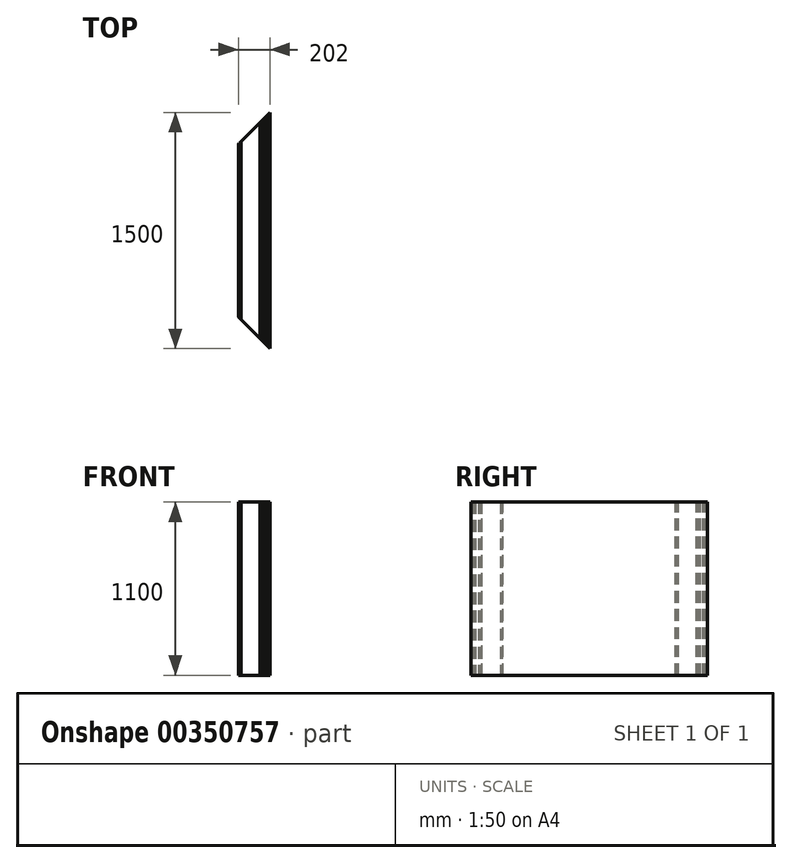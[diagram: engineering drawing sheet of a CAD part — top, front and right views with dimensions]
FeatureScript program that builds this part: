
annotation { "Feature Type Name" : "Feature", "Feature Type Description" : "" }
export const myFeature = defineFeature(function(context is Context, id is Id, definition is map)
    precondition{}
    {
        {
            var Q0;
            Q0=qCreatedBy(makeId("Right.planeOp"),FACE);
            var sketch = newSketch(context, id + "F0", { "sketchPlane" : qUnion([Q0])});
            skLineSegment(sketch, "E0", {"start": v(0, 0) * mm, "end": v(1500, 0) * mm});
            skLineSegment(sketch, "E1", {"start": v(1500, 0) * mm, "end": v(1500, 1100) * mm});
            skLineSegment(sketch, "E2", {"start": v(1500, 1100) * mm, "end": v(0, 1100) * mm});
            skLineSegment(sketch, "E3", {"start": v(0, 1100) * mm, "end": v(0, 0) * mm});
            skSolve(sketch);
        }
        {
            var Q0;
            Q0=makeQuery(id+"F0.imprint","IMPRINT",FACE,{"disambiguationData":[TD([[makeQuery(id+"F0.imprint","IMPRINT",EDGE,{"derivedFrom":sQuery(id+"F0.wireOp",EDGE,"E0")}),1.0]])]});
            extrude(context, id + "F1", {"entities" : qUnion([Q0]), "depth" : 6 * mm});
        }
        {
            var Q0;
            Q0=makeQuery(id+"F1.opExtrude","CAP_FACE",FACE,{"disambiguationData":[OSD([sQuery(id+"F0.wireOp",EDGE,"E0"),sQuery(id+"F0.wireOp",EDGE,"E1"),sQuery(id+"F0.wireOp",EDGE,"E2"),sQuery(id+"F0.wireOp",EDGE,"UxQu33BP-PdVc-IvKo-0Oal-Oq9sfbCTzBfW"),sQuery(id+"F0.wireOp",EDGE,"E3")])],"isStart":false});
            extrude(context, id + "F2", {"entities" : qUnion([Q0]), "depth" : 1 * mm});
        }
        {
            var Q0;
            Q0=makeQuery(id+"F2.opExtrude","CAP_FACE",FACE,{"disambiguationData":[OSD([sQuery(id+"F0.wireOp",EDGE,"E0"),sQuery(id+"F0.wireOp",EDGE,"E1"),sQuery(id+"F0.wireOp",EDGE,"E2"),sQuery(id+"F0.wireOp",EDGE,"UxQu33BP-PdVc-IvKo-0Oal-Oq9sfbCTzBfW"),sQuery(id+"F0.wireOp",EDGE,"E3")])],"isStart":false});
            extrude(context, id + "F3", {"entities" : qUnion([Q0]), "depth" : 10 * mm});
        }
        {
            var Q0;
            Q0=makeQuery(id+"F3.opExtrude","CAP_FACE",FACE,{"disambiguationData":[OSD([sQuery(id+"F0.wireOp",EDGE,"E0"),sQuery(id+"F0.wireOp",EDGE,"E1"),sQuery(id+"F0.wireOp",EDGE,"E2"),sQuery(id+"F0.wireOp",EDGE,"UxQu33BP-PdVc-IvKo-0Oal-Oq9sfbCTzBfW"),sQuery(id+"F0.wireOp",EDGE,"E3")])],"isStart":false});
            extrude(context, id + "F4", {"entities" : qUnion([Q0]), "depth" : 120 * mm});
        }
        {
            var Q0;
            Q0=makeQuery(id+"F4.opExtrude","CAP_FACE",FACE,{"disambiguationData":[OSD([sQuery(id+"F0.wireOp",EDGE,"E0"),sQuery(id+"F0.wireOp",EDGE,"E1"),sQuery(id+"F0.wireOp",EDGE,"E2"),sQuery(id+"F0.wireOp",EDGE,"UxQu33BP-PdVc-IvKo-0Oal-Oq9sfbCTzBfW"),sQuery(id+"F0.wireOp",EDGE,"E3")])],"isStart":false});
            extrude(context, id + "F5", {"entities" : qUnion([Q0]), "depth" : 10 * mm});
        }
        {
            var Q0;
            Q0=makeQuery(id+"F5.opExtrude","CAP_FACE",FACE,{"disambiguationData":[OSD([sQuery(id+"F0.wireOp",EDGE,"E0"),sQuery(id+"F0.wireOp",EDGE,"E1"),sQuery(id+"F0.wireOp",EDGE,"E2"),sQuery(id+"F0.wireOp",EDGE,"UxQu33BP-PdVc-IvKo-0Oal-Oq9sfbCTzBfW"),sQuery(id+"F0.wireOp",EDGE,"E3")])],"isStart":false});
            extrude(context, id + "F6", {"entities" : qUnion([Q0]), "depth" : 10 * mm});
        }
        {
            var Q0;
            Q0=makeQuery(id+"F6.opExtrude","CAP_FACE",FACE,{"disambiguationData":[OSD([sQuery(id+"F0.wireOp",EDGE,"E0"),sQuery(id+"F0.wireOp",EDGE,"E1"),sQuery(id+"F0.wireOp",EDGE,"E2"),sQuery(id+"F0.wireOp",EDGE,"UxQu33BP-PdVc-IvKo-0Oal-Oq9sfbCTzBfW"),sQuery(id+"F0.wireOp",EDGE,"E3")])],"isStart":false});
            extrude(context, id + "F7", {"entities" : qUnion([Q0]), "depth" : 18 * mm});
        }
        {
            var Q0;
            Q0=makeQuery(id+"F7.opExtrude","CAP_FACE",FACE,{"disambiguationData":[OSD([sQuery(id+"F0.wireOp",EDGE,"E0"),sQuery(id+"F0.wireOp",EDGE,"E1"),sQuery(id+"F0.wireOp",EDGE,"E2"),sQuery(id+"F0.wireOp",EDGE,"UxQu33BP-PdVc-IvKo-0Oal-Oq9sfbCTzBfW"),sQuery(id+"F0.wireOp",EDGE,"E3")])],"isStart":false});
            extrude(context, id + "F8", {"entities" : qUnion([Q0]), "depth" : 10 * mm});
        }
        {
            var Q0;
            Q0=makeQuery(id+"F8.opExtrude","CAP_FACE",FACE,{"disambiguationData":[OSD([sQuery(id+"F0.wireOp",EDGE,"E0"),sQuery(id+"F0.wireOp",EDGE,"E1"),sQuery(id+"F0.wireOp",EDGE,"E2"),sQuery(id+"F0.wireOp",EDGE,"E3")])],"isStart":false});
            extrude(context, id + "F9", {"entities" : qUnion([Q0]), "depth" : 1 * mm});
        }
        {
            var Q0;
            Q0=makeQuery(id+"F9.opExtrude","CAP_FACE",FACE,{"disambiguationData":[OSD([sQuery(id+"F0.wireOp",EDGE,"E0"),sQuery(id+"F0.wireOp",EDGE,"E1"),sQuery(id+"F0.wireOp",EDGE,"E2"),sQuery(id+"F0.wireOp",EDGE,"E3")])],"isStart":false});
            var sketch = newSketch(context, id + "F10", { "sketchPlane" : qUnion([Q0])});
            skLineSegment(sketch, "E4.bottom", {"start": v(0, 0) * mm, "end": v(70, 0) * mm});
            skLineSegment(sketch, "E4.top", {"start": v(0, 1100) * mm, "end": v(70, 1100) * mm});
            skLineSegment(sketch, "E4.left", {"start": v(0, 0) * mm, "end": v(0, 1100) * mm});
            skLineSegment(sketch, "E4.right", {"start": v(70, 0) * mm, "end": v(70, 1100) * mm});
            skLineSegment(sketch, "E5.bottom", {"start": v(1500, 0) * mm, "end": v(1430, 0) * mm});
            skLineSegment(sketch, "E5.top", {"start": v(1500, 1100) * mm, "end": v(1430, 1100) * mm});
            skLineSegment(sketch, "E5.left", {"start": v(1500, 0) * mm, "end": v(1500, 1100) * mm});
            skLineSegment(sketch, "E5.right", {"start": v(1430, 0) * mm, "end": v(1430, 1100) * mm});
            skSolve(sketch);
        }
        {
            var Q0;
            Q0 = qSketchRegion(id + "F10", true);
            extrude(context, id + "F11", {"entities" : qUnion([Q0]), "depth" : 8 * mm});
        }
        {
            var Q0;
            Q0=makeQuery(id+"F11.opExtrude","CAP_FACE",FACE,{"disambiguationData":[OSD([sQuery(id+"F10.wireOp",EDGE,"E4.bottom"),sQuery(id+"F10.wireOp",EDGE,"E4.top"),sQuery(id+"F10.wireOp",EDGE,"E4.left"),sQuery(id+"F10.wireOp",EDGE,"E4.right")])],"isStart":false});
            var sketch = newSketch(context, id + "F12", { "sketchPlane" : qUnion([Q0])});
            skLineSegment(sketch, "E6.bottom", {"start": v(0, 0) * mm, "end": v(1500, 0) * mm});
            skLineSegment(sketch, "E6.top", {"start": v(0, 1100) * mm, "end": v(1500, 1100) * mm});
            skLineSegment(sketch, "E6.left", {"start": v(0, 0) * mm, "end": v(0, 1100) * mm});
            skLineSegment(sketch, "E6.right", {"start": v(1500, 0) * mm, "end": v(1500, 1100) * mm});
            skSolve(sketch);
        }
        {
            var Q0;
            Q0 = qSketchRegion(id + "F12", true);
            extrude(context, id + "F13", {"entities" : qUnion([Q0]), "depth" : 8 * mm});
        }
        {
            var Q0;
            Q0=makeQuery(id+"F4.opExtrude","SWEPT_FACE",FACE,{"disambiguationData":[OSD([sQuery(id+"F0.wireOp",EDGE,"E2")])]});
            var sketch = newSketch(context, id + "F14", { "sketchPlane" : qUnion([Q0])});
            skLineSegment(sketch, "E7", {"start": v(202, 1500) * mm, "end": v(0, 1298) * mm});
            skLineSegment(sketch, "E8", {"start": v(0, 1298) * mm, "end": v(0, 1500) * mm});
            skLineSegment(sketch, "E9", {"start": v(0, 1500) * mm, "end": v(202, 1500) * mm});
            skLineSegment(sketch, "E10", {"start": v(0, 202) * mm, "end": v(202, 0) * mm});
            skLineSegment(sketch, "E11", {"start": v(202, 0) * mm, "end": v(0, 0) * mm});
            skLineSegment(sketch, "E12", {"start": v(0, 0) * mm, "end": v(0, 202) * mm});
            skSolve(sketch);
        }
        {
            var Q0;
            Q0 = qSketchRegion(id + "F14", true);
            extrude(context, id + "F15", {"entities" : qUnion([Q0]), "operationType" : NewBodyOperationType.REMOVE, "endBound" : BoundingType.THROUGH_ALL, "oppositeDirection" : true, "depth" : 25 * mm});
        }
    });
